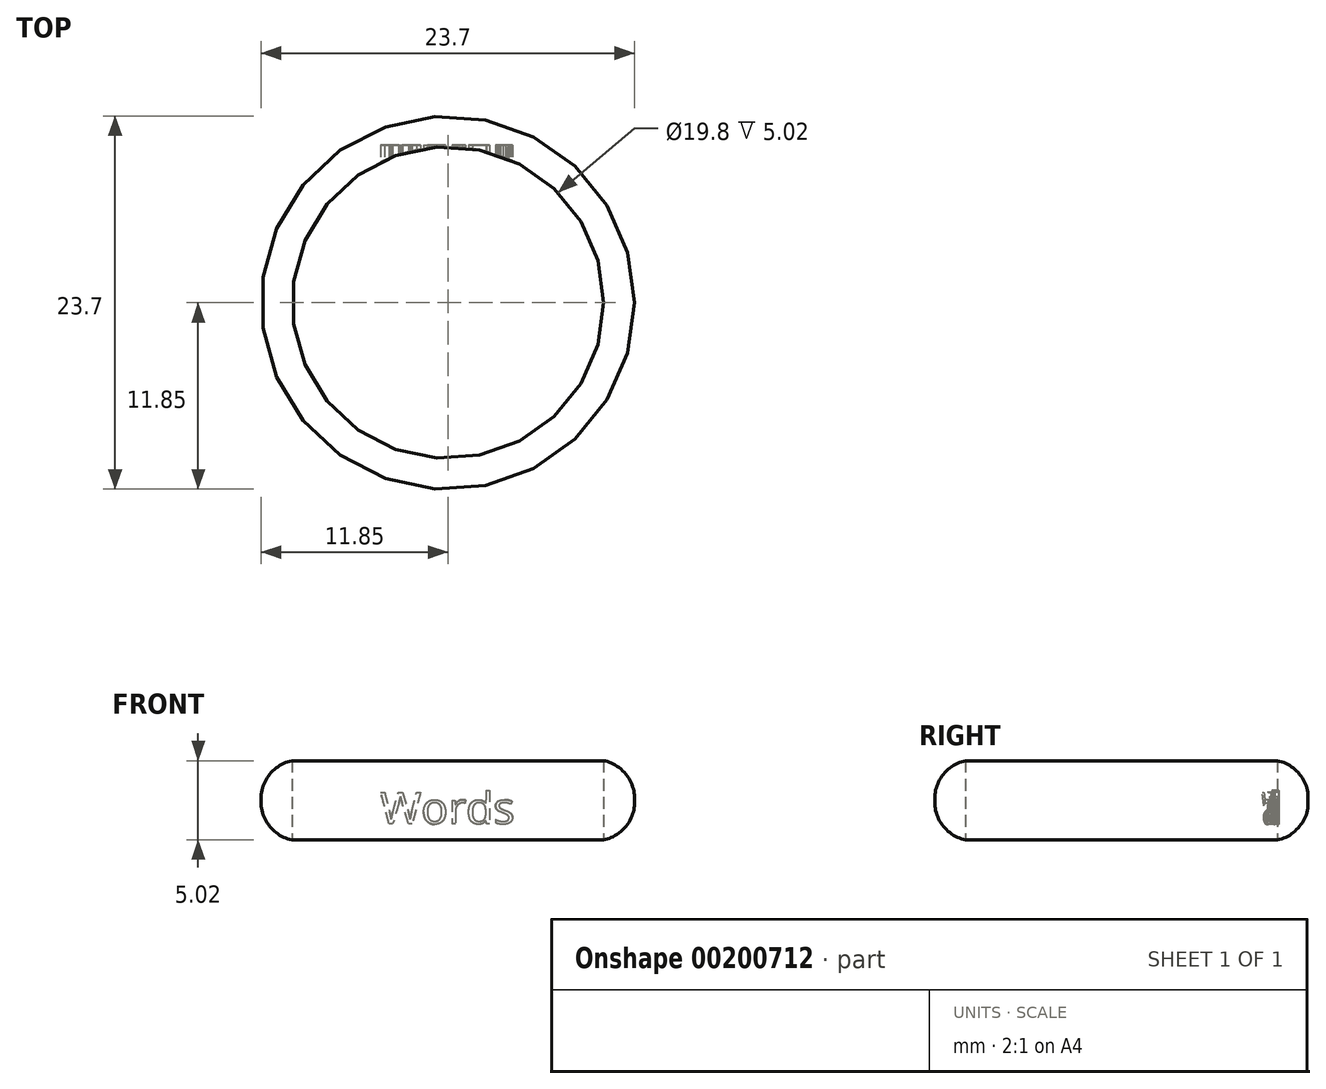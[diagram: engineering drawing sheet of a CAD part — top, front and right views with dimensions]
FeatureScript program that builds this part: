
annotation { "Feature Type Name" : "Feature", "Feature Type Description" : "" }
export const myFeature = defineFeature(function(context is Context, id is Id, definition is map)
    precondition{}
    {
        {
            var Q0;
            Q0=qCreatedBy(makeId("Top.planeOp"),FACE);
            var sketch = newSketch(context, id + "F0", { "sketchPlane" : qUnion([Q0])});
            skCircle(sketch, "E0", {"center": v(0, 0) * mm, "radius": 9.9 * mm});
            skCircle(sketch, "E1.0", {"center": v(0, 0) * mm, "radius": 11.85 * mm});
            skSolve(sketch);
        }
        {
            var Q0;
            Q0 = qSketchRegion(id + "F0", true);
            extrude(context, id + "F1", {"entities" : qUnion([Q0]), "depth" : 5.02 * mm});
        }
        {
            var Q0;
            Q0=makeQuery(id+"F1.opExtrude","SWEPT_FACE",FACE,{"disambiguationData":[OSD([sQuery(id+"F0.wireOp",EDGE,"E1.0")])]});
            fillet(context, id + "F2", {"entities" : qUnion([Q0]), "radius" : 2.3 * mm, "tangentPropagation" : true, "rho" : 0.4, "crossSection" : FilletCrossSection.CONIC, "allowEdgeOverflow" : false});
        }
        {
            var Q0;
            Q0=qCreatedBy(makeId("Front.planeOp"),FACE);
            var sketch = newSketch(context, id + "F3", { "sketchPlane" : qUnion([Q0])});
            skText(sketch, "E2", { "text": "Words", "fontName": "OpenSans-Regular.ttf"});
            const initialGuessF3  = {"E2": [-0.0043, 0.00101, 1, 0, 0.00203]};
            skSetInitialGuess(sketch, initialGuessF3);
            skSolve(sketch);
        }
        {
            var Q0;
            Q0 = qSketchRegion(id + "F3", true);
            extrude(context, id + "F4", {"entities" : qUnion([Q0]), "operationType" : NewBodyOperationType.REMOVE, "oppositeDirection" : true, "depth" : 10 * mm});
        }
    });
